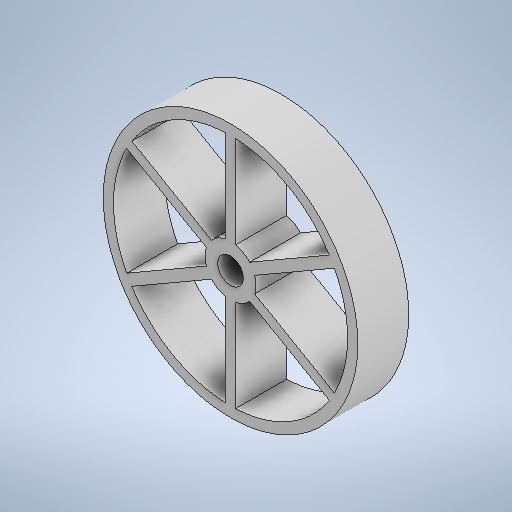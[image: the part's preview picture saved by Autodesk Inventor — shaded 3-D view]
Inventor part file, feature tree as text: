
AUTODESK INVENTOR PART (.ipt)
format: ipt  version: 2025 (Build 290162000, 162)  size: 278,528 bytes
history: native  units: mm
features: extrude x2, sketch x2, other x1, pattern_circular x1
ambient origin geometry x8: Origin, YZ Plane, XZ Plane, XY Plane, X Axis, Y Axis, Z Axis, Center Point
bodies: Body1 (feature_tree)
feature tree (6):
  other  "ソリッド1"
  extrude  "押し出し1"  Depth=50.0mm
  extrude  "押し出し2"  Depth=2.0mm
  pattern_circular  "円形状パターン1"  [2 undecoded]
  sketch  "スケッチ1"
  sketch  "スケッチ2"
note: 2 required parameter values undecoded (feature->parameter linkage not recoverable at this tier; creation-order binding heuristic only, values carry confidence <= 0.55)
